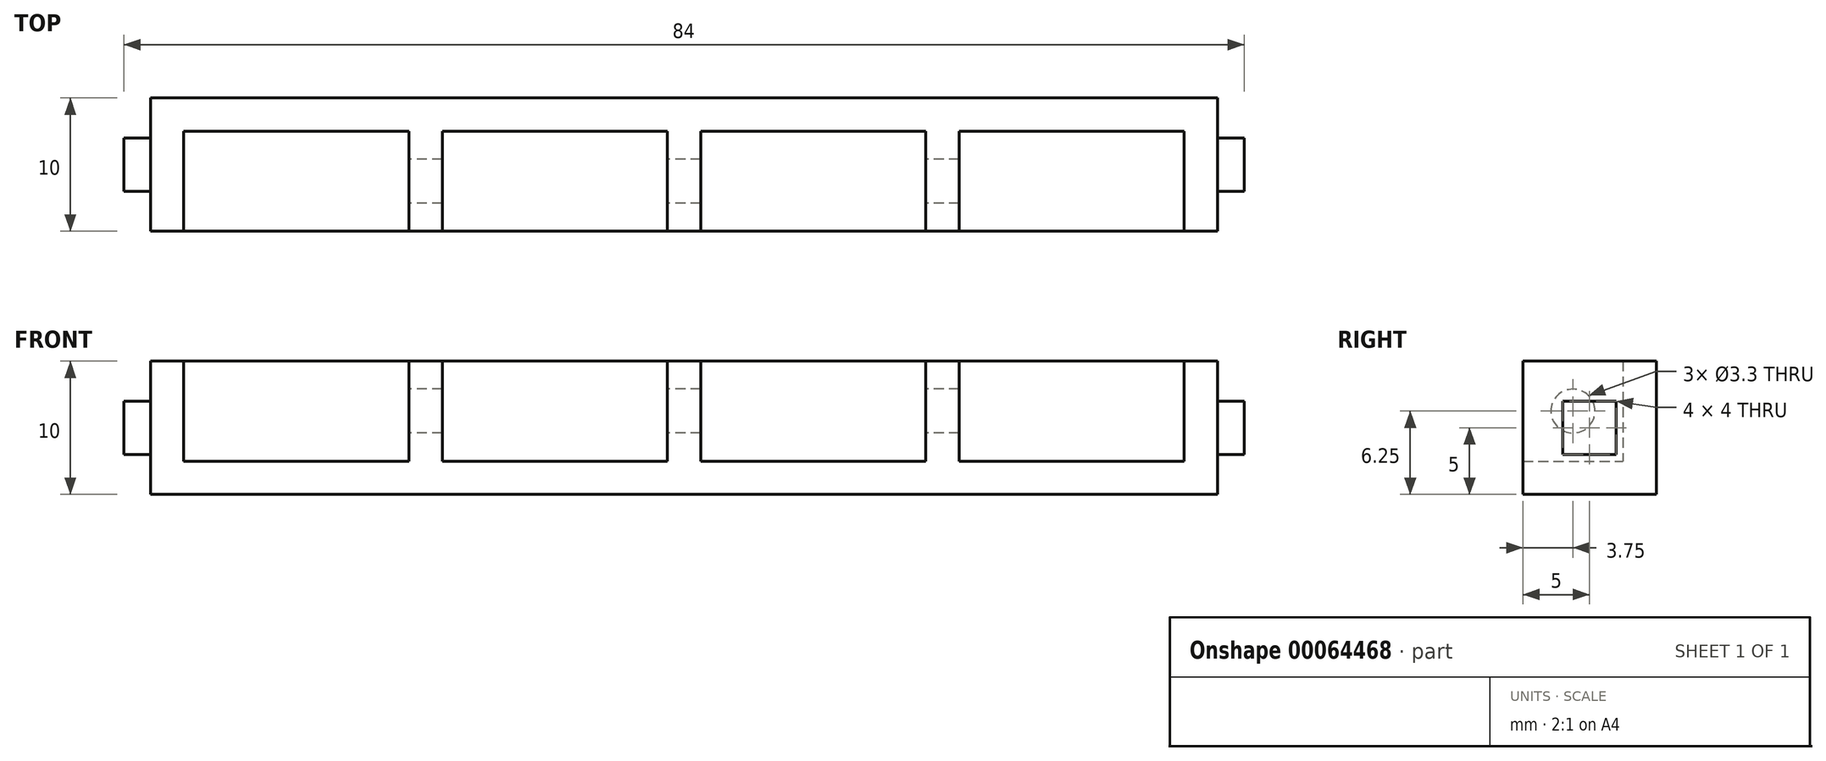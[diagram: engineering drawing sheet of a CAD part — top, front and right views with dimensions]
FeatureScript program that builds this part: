
annotation { "Feature Type Name" : "Feature", "Feature Type Description" : "" }
export const myFeature = defineFeature(function(context is Context, id is Id, definition is map)
    precondition{}
    {
        {
            var Q0;
            Q0=qCreatedBy(makeId("Top.planeOp"),FACE);
            var sketch = newSketch(context, id + "F0", { "sketchPlane" : qUnion([Q0])});
            skLineSegment(sketch, "E0.rect.bottom", {"start": v(40, -5) * mm, "end": v(-40, -5) * mm});
            skLineSegment(sketch, "E0.rect.top", {"start": v(40, 5) * mm, "end": v(-40, 5) * mm});
            skLineSegment(sketch, "E0.rect.left", {"start": v(40, -5) * mm, "end": v(40, 5) * mm});
            skLineSegment(sketch, "E0.rect.right", {"start": v(-40, -5) * mm, "end": v(-40, 5) * mm});
            skPoint(sketch, "E0.rect.middle", {"position": v(0, 0) * mm});
            skSolve(sketch);
        }
        {
            var Q0;
            Q0=makeQuery(id+"F0.imprint","IMPRINT",FACE,{"disambiguationData":[TD([[makeQuery(id+"F0.imprint","IMPRINT",EDGE,{"derivedFrom":sQuery(id+"F0.wireOp",EDGE,"E0.rect.bottom")}),-1.0]])]});
            extrude(context, id + "F1", {"entities" : qUnion([Q0]), "depth" : 10 * mm});
        }
        {
            var Q0;
            Q0=makeQuery(id+"F1.opExtrude","SWEPT_FACE",FACE,{"disambiguationData":[OSD([sQuery(id+"F0.wireOp",EDGE,"E0.rect.left")])]});
            var sketch = newSketch(context, id + "F2", { "sketchPlane" : qUnion([Q0])});
            skLineSegment(sketch, "E1.0", {"start": v(-2, 3) * mm, "end": v(2, 3) * mm});
            skLineSegment(sketch, "E1.1", {"start": v(-2, 7) * mm, "end": v(-2, 3) * mm});
            skLineSegment(sketch, "E1.2", {"start": v(2, 7) * mm, "end": v(-2, 7) * mm});
            skLineSegment(sketch, "E1.3", {"start": v(2, 3) * mm, "end": v(2, 7) * mm});
            skSolve(sketch);
        }
        {
            var Q0;
            Q0 = qSketchRegion(id + "F2", true);
            var Q1;
            Q1=makeQuery(id+"F2.imprint","IMPRINT",FACE,{"disambiguationData":[TD([[makeQuery(id+"F2.imprint","IMPRINT",EDGE,{"derivedFrom":sQuery(id+"F2.wireOp",EDGE,"E1.0")}),1.0]])]});
            extrude(context, id + "F3", {"entities" : qUnion([Q0, Q1]), "operationType" : NewBodyOperationType.ADD, "depth" : 2 * mm});
        }
        {
            var Q0;
            Q0=makeQuery(id+"F1.opExtrude","SWEPT_FACE",FACE,{"disambiguationData":[OSD([sQuery(id+"F0.wireOp",EDGE,"E0.rect.right")])]});
            var sketch = newSketch(context, id + "F4", { "sketchPlane" : qUnion([Q0])});
            skLineSegment(sketch, "E2.0", {"start": v(-2, 3) * mm, "end": v(2, 3) * mm});
            skLineSegment(sketch, "E2.1", {"start": v(-2, 7) * mm, "end": v(-2, 3) * mm});
            skLineSegment(sketch, "E2.2", {"start": v(2, 7) * mm, "end": v(-2, 7) * mm});
            skLineSegment(sketch, "E2.3", {"start": v(2, 3) * mm, "end": v(2, 7) * mm});
            skSolve(sketch);
        }
        {
            var Q0;
            Q0=makeQuery(id+"F4.imprint","IMPRINT",FACE,{"disambiguationData":[TD([[makeQuery(id+"F4.imprint","IMPRINT",EDGE,{"derivedFrom":sQuery(id+"F4.wireOp",EDGE,"E2.0")}),1.0]])]});
            extrude(context, id + "F5", {"entities" : qUnion([Q0]), "operationType" : NewBodyOperationType.ADD, "depth" : 2 * mm});
        }
        {
            var Q0;
            Q0=makeQuery(id+"F1.opExtrude","SWEPT_FACE",FACE,{"disambiguationData":[OSD([sQuery(id+"F0.wireOp",EDGE,"E0.rect.bottom")])]});
            var Q1;
            Q1=makeQuery(id+"F1.opExtrude","CAP_FACE",FACE,{"disambiguationData":[OSD([sQuery(id+"F0.wireOp",EDGE,"E0.rect.bottom"),sQuery(id+"F0.wireOp",EDGE,"E0.rect.top"),sQuery(id+"F0.wireOp",EDGE,"E0.rect.left"),sQuery(id+"F0.wireOp",EDGE,"E0.rect.right")])],"isStart":false});
            shell(context, id + "F6", {"entities" : qUnion([Q0, Q1]), "thickness" : 2.5 * mm});
        }
        {
            var Q0;
            Q0=makeQuery(id+"F6.opShell","OFFSET_FACE",FACE,{"disambiguationData":[OSD([sQuery(id+"F0.wireOp",EDGE,"E0.rect.bottom"),sQuery(id+"F0.wireOp",EDGE,"E0.rect.top"),sQuery(id+"F0.wireOp",EDGE,"E0.rect.left"),sQuery(id+"F0.wireOp",EDGE,"E0.rect.right")])]});
            var sketch = newSketch(context, id + "F7", { "sketchPlane" : qUnion([Q0])});
            skLineSegment(sketch, "E3.rect.bottom", {"start": v(-1.25, -5) * mm, "end": v(1.25, -5) * mm});
            skLineSegment(sketch, "E3.rect.top", {"start": v(-1.25, 2.5) * mm, "end": v(1.25, 2.5) * mm});
            skLineSegment(sketch, "E3.rect.left", {"start": v(-1.25, -5) * mm, "end": v(-1.25, 2.5) * mm});
            skLineSegment(sketch, "E3.rect.right", {"start": v(1.25, -5) * mm, "end": v(1.25, 2.5) * mm});
            skPoint(sketch, "E3.rect.middle", {"position": v(0, -1.25) * mm});
            skLineSegment(sketch, "E4.rect.bottom", {"start": v(-18.12, -5) * mm, "end": v(-20.62, -5) * mm});
            skLineSegment(sketch, "E4.rect.top", {"start": v(-18.12, 2.5) * mm, "end": v(-20.62, 2.5) * mm});
            skLineSegment(sketch, "E4.rect.left", {"start": v(-18.12, -5) * mm, "end": v(-18.12, 2.5) * mm});
            skLineSegment(sketch, "E4.rect.right", {"start": v(-20.62, -5) * mm, "end": v(-20.62, 2.5) * mm});
            skPoint(sketch, "E4.rect.middle", {"position": v(-19.38, -1.25) * mm});
            skLineSegment(sketch, "E5.rect.bottom", {"start": v(20.63, -5) * mm, "end": v(18.13, -5) * mm});
            skLineSegment(sketch, "E5.rect.top", {"start": v(20.63, 2.5) * mm, "end": v(18.13, 2.5) * mm});
            skLineSegment(sketch, "E5.rect.left", {"start": v(20.63, -5) * mm, "end": v(20.63, 2.5) * mm});
            skLineSegment(sketch, "E5.rect.right", {"start": v(18.13, -5) * mm, "end": v(18.13, 2.5) * mm});
            skPoint(sketch, "E5.rect.middle", {"position": v(19.38, -1.25) * mm});
            skPoint(sketch, "E6.orphan", {"position": v(-1.25, -1.25) * mm});
            skPoint(sketch, "E7.orphan", {"position": v(-37.5, -1.25) * mm});
            skPoint(sketch, "E8.orphan", {"position": v(37.5, -1.25) * mm});
            skPoint(sketch, "E9.orphan", {"position": v(1.25, -1.25) * mm});
            skSolve(sketch);
        }
        {
            var Q0;
            Q0=makeQuery(id+"F7.imprint","IMPRINT",FACE,{"disambiguationData":[TD([[makeQuery(id+"F7.imprint","IMPRINT",EDGE,{"derivedFrom":sQuery(id+"F7.wireOp",EDGE,"E4.rect.bottom")}),-1.0]])]});
            var Q1;
            Q1=makeQuery(id+"F7.imprint","IMPRINT",FACE,{"disambiguationData":[TD([[makeQuery(id+"F7.imprint","IMPRINT",EDGE,{"derivedFrom":sQuery(id+"F7.wireOp",EDGE,"E3.rect.bottom")}),-1.0]])]});
            var Q2;
            Q2=makeQuery(id+"F7.imprint","IMPRINT",FACE,{"disambiguationData":[TD([[makeQuery(id+"F7.imprint","IMPRINT",EDGE,{"derivedFrom":sQuery(id+"F7.wireOp",EDGE,"E5.rect.bottom")}),-1.0]])]});
            var Q3;
            Q3=makeQuery(id+"F1.opExtrude","CAP_FACE",FACE,{"disambiguationData":[OSD([sQuery(id+"F0.wireOp",EDGE,"E0.rect.bottom"),sQuery(id+"F0.wireOp",EDGE,"E0.rect.top"),sQuery(id+"F0.wireOp",EDGE,"E0.rect.left"),sQuery(id+"F0.wireOp",EDGE,"E0.rect.right")])],"isStart":false});
            extrude(context, id + "F8", {"entities" : qUnion([Q0, Q1, Q2]), "operationType" : NewBodyOperationType.ADD, "endBound" : BoundingType.UP_TO_SURFACE, "endBoundEntityFace" : qUnion([Q3]), "depth" : 25 * mm});
        }
        {
            var Q0;
            Q0=makeQuery(id+"F8.opExtrude","SWEPT_FACE",FACE,{"disambiguationData":[OSD([sQuery(id+"F7.wireOp",EDGE,"E4.rect.right")])]});
            var sketch = newSketch(context, id + "F9", { "sketchPlane" : qUnion([Q0])});
            skLineSegment(sketch, "E10", {"start": v(-2.5, 6.25) * mm, "end": v(5, 6.25) * mm, "construction": true});
            skCircle(sketch, "E11", {"center": v(1.25, 6.25) * mm, "radius": 1.65 * mm});
            skSolve(sketch);
        }
        {
            var Q0;
            Q0=makeQuery(id+"F9.imprint","IMPRINT",FACE,{"disambiguationData":[TD([[makeQuery(id+"F9.imprint","IMPRINT",EDGE,{"derivedFrom":sQuery(id+"F9.wireOp",EDGE,"E11")}),1.0]])]});
            var Q1;
            Q1=makeQuery(id+"F8.opExtrude","SWEPT_FACE",FACE,{"disambiguationData":[OSD([sQuery(id+"F7.wireOp",EDGE,"E5.rect.left")])]});
            extrude(context, id + "F10", {"entities" : qUnion([Q0]), "operationType" : NewBodyOperationType.REMOVE, "endBound" : BoundingType.UP_TO_SURFACE, "oppositeDirection" : true, "endBoundEntityFace" : qUnion([Q1]), "depth" : 25 * mm});
        }
    });
